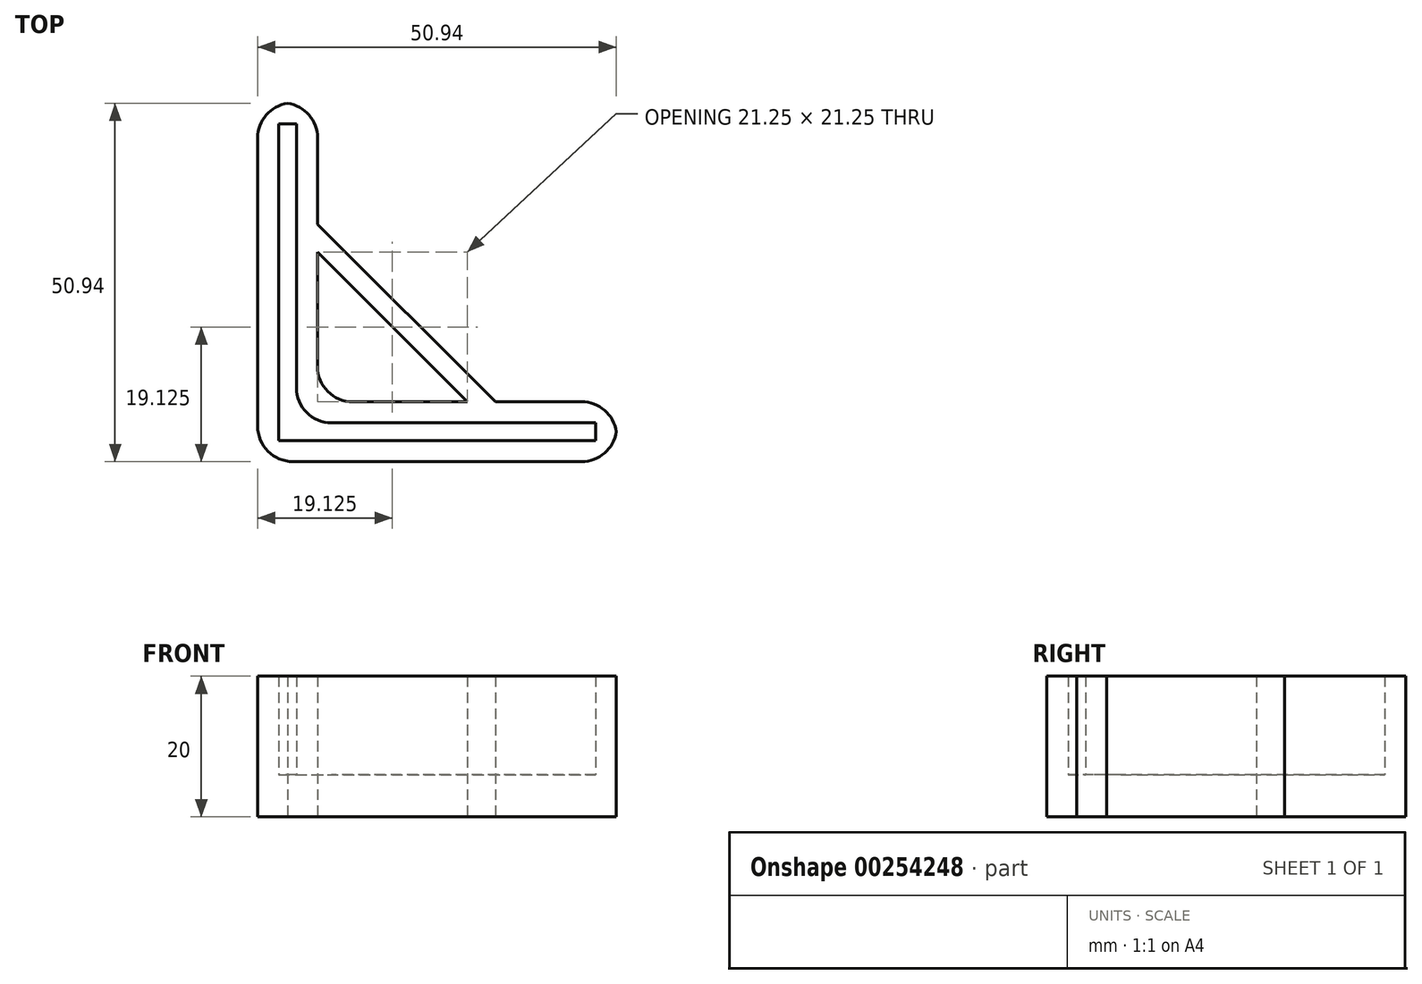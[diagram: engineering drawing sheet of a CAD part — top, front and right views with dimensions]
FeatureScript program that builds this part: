
annotation { "Feature Type Name" : "Feature", "Feature Type Description" : "" }
export const myFeature = defineFeature(function(context is Context, id is Id, definition is map)
    precondition{}
    {
        {
            var Q0;
            Q0=qCreatedBy(makeId("Top.planeOp"),FACE);
            var sketch = newSketch(context, id + "F0", { "sketchPlane" : qUnion([Q0])});
            skLineSegment(sketch, "E0", {"start": v(0, 45) * mm, "end": v(0, 0) * mm});
            skLineSegment(sketch, "E1", {"start": v(0, 0) * mm, "end": v(45, 0) * mm});
            skLineSegment(sketch, "E2", {"start": v(45, 0) * mm, "end": v(45, 2.5) * mm});
            skLineSegment(sketch, "E3", {"start": v(45, 2.5) * mm, "end": v(2.5, 2.5) * mm});
            skLineSegment(sketch, "E4", {"start": v(2.5, 2.5) * mm, "end": v(2.5, 45) * mm});
            skLineSegment(sketch, "E5", {"start": v(2.5, 45) * mm, "end": v(0, 45) * mm});
            skLineSegment(sketch, "E6.0", {"start": v(5.5, 48) * mm, "end": v(-3, 48) * mm});
            skLineSegment(sketch, "E6.1", {"start": v(-3, -3) * mm, "end": v(48, -3) * mm});
            skLineSegment(sketch, "E6.2", {"start": v(48, -3) * mm, "end": v(48, 5.5) * mm});
            skLineSegment(sketch, "E6.3", {"start": v(-3, 48) * mm, "end": v(-3, -3) * mm});
            skLineSegment(sketch, "E6.4", {"start": v(48, 5.5) * mm, "end": v(5.5, 5.5) * mm});
            skLineSegment(sketch, "E6.5", {"start": v(5.5, 5.5) * mm, "end": v(5.5, 48) * mm});
            skLineSegment(sketch, "E7", {"start": v(5.5, 26.75) * mm, "end": v(26.75, 5.5) * mm});
            skLineSegment(sketch, "E8", {"start": v(5.5, 30.75) * mm, "end": v(30.75, 5.5) * mm});
            skSolve(sketch);
        }
        {
            var Q0;
            Q0 = qSketchRegion(id + "F0", true);
            extrude(context, id + "F1", {"entities" : qUnion([Q0]), "depth" : 20 * mm});
        }
        {
            var Q0;
            Q0=makeQuery(id+"F0.imprint","IMPRINT",FACE,{"disambiguationData":[TD([[makeQuery(id+"F0.imprint","IMPRINT",EDGE,{"derivedFrom":sQuery(id+"F0.wireOp",EDGE,"E0")}),1.0]])]});
            extrude(context, id + "F2", {"entities" : qUnion([Q0]), "operationType" : NewBodyOperationType.ADD, "depth" : 6 * mm});
        }
        {
            var Q0;
            Q0=makeQuery(id+"F1.opExtrude","SWEPT_EDGE",EDGE,{"disambiguationData":[OSD([sQuery(id+"F0.wireOp",EDGE,"E6.4"),sQuery(id+"F0.wireOp",EDGE,"E6.5")])]});
            var Q1;
            Q1=makeQuery(id+"F1.opExtrude","SWEPT_EDGE",EDGE,{"disambiguationData":[OSD([sQuery(id+"F0.wireOp",EDGE,"E6.2"),sQuery(id+"F0.wireOp",EDGE,"E6.4")])]});
            var Q2;
            Q2=makeQuery(id+"F1.opExtrude","SWEPT_EDGE",EDGE,{"disambiguationData":[OSD([sQuery(id+"F0.wireOp",EDGE,"E6.1"),sQuery(id+"F0.wireOp",EDGE,"E6.2")])]});
            var Q3;
            Q3=makeQuery(id+"F1.opExtrude","SWEPT_EDGE",EDGE,{"disambiguationData":[OSD([sQuery(id+"F0.wireOp",EDGE,"E6.0"),sQuery(id+"F0.wireOp",EDGE,"E6.5")])]});
            var Q4;
            Q4=makeQuery(id+"F1.opExtrude","SWEPT_EDGE",EDGE,{"disambiguationData":[OSD([sQuery(id+"F0.wireOp",EDGE,"E6.0"),sQuery(id+"F0.wireOp",EDGE,"E6.3")])]});
            var Q5;
            Q5=makeQuery(id+"F1.opExtrude","SWEPT_EDGE",EDGE,{"disambiguationData":[OSD([sQuery(id+"F0.wireOp",EDGE,"E6.1"),sQuery(id+"F0.wireOp",EDGE,"E6.3")])]});
            fillet(context, id + "F3", {"entities" : qUnion([Q0, Q1, Q2, Q3, Q4, Q5]), "radius" : 5 * mm, "tangentPropagation" : true, "allowEdgeOverflow" : false});
        }
        {
            var Q0;
            Q0=makeQuery(id+"F1.opExtrude","SWEPT_EDGE",EDGE,{"disambiguationData":[OSD([sQuery(id+"F0.wireOp",EDGE,"E3"),sQuery(id+"F0.wireOp",EDGE,"E4")])]});
            fillet(context, id + "F4", {"entities" : qUnion([Q0]), "radius" : 5 * mm, "tangentPropagation" : true, "allowEdgeOverflow" : false});
        }
    });
